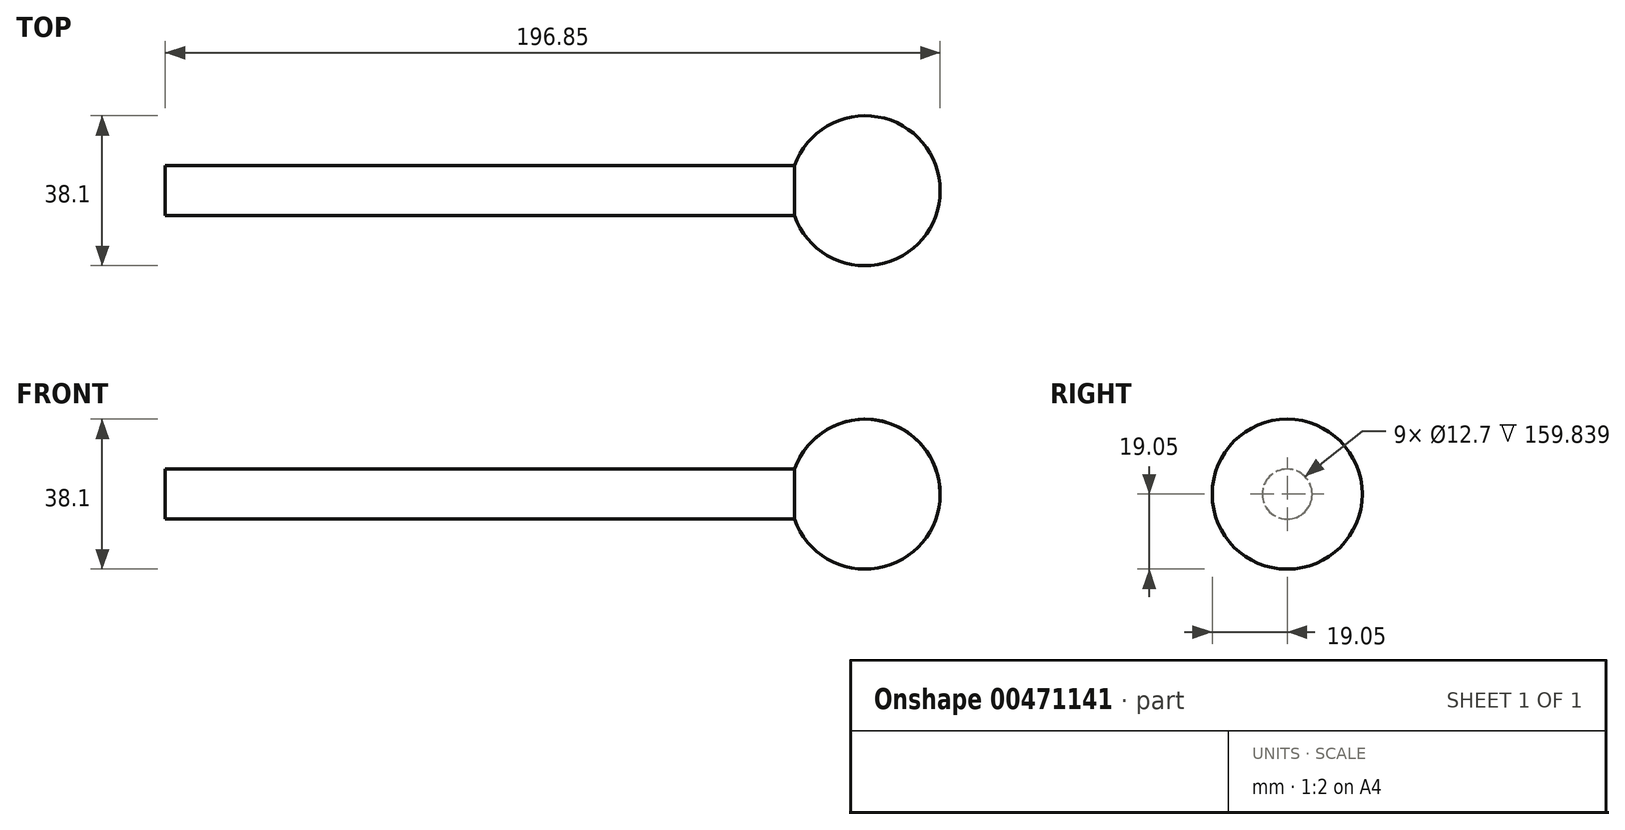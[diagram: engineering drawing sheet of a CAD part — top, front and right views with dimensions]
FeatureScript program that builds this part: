
annotation { "Feature Type Name" : "Feature", "Feature Type Description" : "" }
export const myFeature = defineFeature(function(context is Context, id is Id, definition is map)
    precondition{}
    {
        {
            var Q0;
            Q0=qCreatedBy(makeId("Front.planeOp"),FACE);
            var sketch = newSketch(context, id + "F0", { "sketchPlane" : qUnion([Q0])});
            skLineSegment(sketch, "E0", {"start": v(0, 0) * mm, "end": v(0, 6.35) * mm});
            skLineSegment(sketch, "E1", {"start": v(0, 6.35) * mm, "end": v(159.84, 6.35) * mm});
            skArc(sketch, "E2", {"start": v(196.85, 0) * mm, "mid": v(181.02, 18.78) * mm, "end": v(159.84, 6.35) * mm});
            skLineSegment(sketch, "E3", {"start": v(0, 0) * mm, "end": v(196.85, 0) * mm});
            skSolve(sketch);
        }
        {
            var Q0;
            Q0=sQuery(id+"F0.wireOp",EDGE,"E1");
            var Q1;
            Q1=sQuery(id+"F0.wireOp",EDGE,"E2");
            var Q2;
            Q2=sQuery(id+"F0.wireOp",EDGE,"E0");
            var Q3;
            Q3=sQuery(id+"F0.wireOp",EDGE,"E3");
            revolve(context, id + "F1", {"bodyType" : ToolBodyType.SURFACE, "surfaceEntities" : qUnion([Q0, Q1, Q2]), "axis" : qUnion([Q3]), "revolveType" : RevolveType.FULL});
        }
    });
